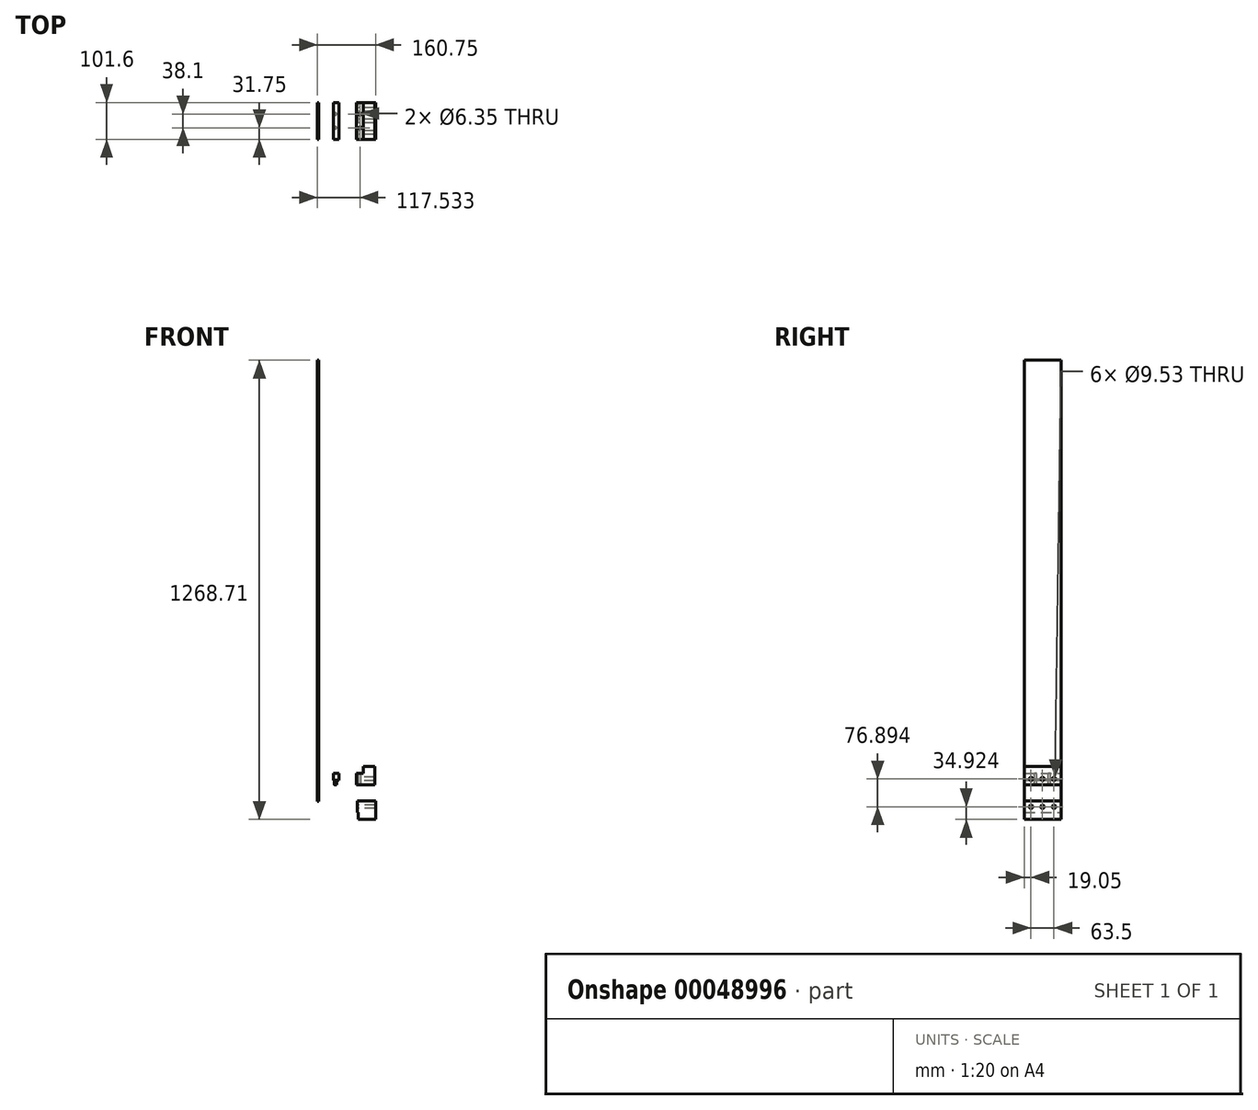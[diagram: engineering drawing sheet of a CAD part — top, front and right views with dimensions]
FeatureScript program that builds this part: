
annotation { "Feature Type Name" : "Feature", "Feature Type Description" : "" }
export const myFeature = defineFeature(function(context is Context, id is Id, definition is map)
    precondition{}
    {
        {
            var Q0;
            Q0=qCreatedBy(makeId("Front.planeOp"),FACE);
            var sketch = newSketch(context, id + "F0", { "sketchPlane" : qUnion([Q0])});
            skLineSegment(sketch, "E0", {"start": v(-61, 60.92) * mm, "end": v(-61, 29.17) * mm});
            skLineSegment(sketch, "E1", {"start": v(-61, 29.17) * mm, "end": v(-10.2, 29.17) * mm});
            skLineSegment(sketch, "E2", {"start": v(-10.2, 29.17) * mm, "end": v(-10.2, 79.97) * mm});
            skLineSegment(sketch, "E3", {"start": v(-10.2, 79.97) * mm, "end": v(-41.94, 79.97) * mm});
            skLineSegment(sketch, "E4", {"start": v(-41.94, 79.97) * mm, "end": v(-41.94, 60.92) * mm});
            skLineSegment(sketch, "E5", {"start": v(-41.94, 60.92) * mm, "end": v(-61, 60.92) * mm});
            skLineSegment(sketch, "E6", {"start": v(-59.05, -15.97) * mm, "end": v(-59.05, -47.72) * mm});
            skLineSegment(sketch, "E7", {"start": v(-59.05, -47.72) * mm, "end": v(-55.87, -47.72) * mm});
            skLineSegment(sketch, "E8", {"start": v(-55.87, -47.72) * mm, "end": v(-55.87, -66.77) * mm});
            skLineSegment(sketch, "E9", {"start": v(-55.87, -66.77) * mm, "end": v(-8.25, -66.77) * mm});
            skLineSegment(sketch, "E10", {"start": v(-8.25, -66.77) * mm, "end": v(-8.25, -15.97) * mm});
            skLineSegment(sketch, "E11", {"start": v(-8.25, -15.97) * mm, "end": v(-59.05, -15.97) * mm});
            skLineSegment(sketch, "E12.bottom", {"start": v(-125.4, 59.88) * mm, "end": v(-109.52, 59.88) * mm});
            skLineSegment(sketch, "E12.top", {"start": v(-125.4, 40.83) * mm, "end": v(-109.52, 40.83) * mm});
            skLineSegment(sketch, "E12.left", {"start": v(-125.4, 59.88) * mm, "end": v(-125.4, 40.83) * mm});
            skLineSegment(sketch, "E12.right", {"start": v(-109.52, 59.88) * mm, "end": v(-109.52, 40.83) * mm});
            skSolve(sketch);
        }
        {
            var Q0;
            Q0=makeQuery(id+"F0.imprint","IMPRINT",FACE,{"disambiguationData":[TD([[makeQuery(id+"F0.imprint","IMPRINT",EDGE,{"derivedFrom":sQuery(id+"F0.wireOp",EDGE,"E12.bottom")}),-1.0]])]});
            extrude(context, id + "F1", {"entities" : qUnion([Q0]), "depth" : 101.6 * mm});
        }
        {
            var Q0;
            Q0=makeQuery(id+"F0.imprint","IMPRINT",FACE,{"disambiguationData":[TD([[makeQuery(id+"F0.imprint","IMPRINT",EDGE,{"derivedFrom":sQuery(id+"F0.wireOp",EDGE,"E0")}),1.0]])]});
            extrude(context, id + "F2", {"entities" : qUnion([Q0]), "depth" : 101.6 * mm});
        }
        {
            var Q0;
            Q0=makeQuery(id+"F0.imprint","IMPRINT",FACE,{"disambiguationData":[TD([[makeQuery(id+"F0.imprint","IMPRINT",EDGE,{"derivedFrom":sQuery(id+"F0.wireOp",EDGE,"E6")}),1.0]])]});
            extrude(context, id + "F3", {"entities" : qUnion([Q0]), "depth" : 101.6 * mm});
        }
        {
            var Q0;
            Q0=makeQuery(id+"F2.opExtrude","SWEPT_FACE",FACE,{"disambiguationData":[OSD([sQuery(id+"F0.wireOp",EDGE,"E5")])]});
            var sketch = newSketch(context, id + "F4", { "sketchPlane" : qUnion([Q0])});
            skLineSegment(sketch, "E13.bottom", {"start": v(-61, -101.6) * mm, "end": v(-51.47, -101.6) * mm});
            skLineSegment(sketch, "E13.top", {"start": v(-61, -69.85) * mm, "end": v(-51.47, -69.85) * mm});
            skLineSegment(sketch, "E13.left", {"start": v(-61, -101.6) * mm, "end": v(-61, -69.85) * mm});
            skLineSegment(sketch, "E13.right", {"start": v(-51.47, -101.6) * mm, "end": v(-51.47, -69.85) * mm});
            skLineSegment(sketch, "E14.bottom", {"start": v(-61, 0) * mm, "end": v(-51.47, 0) * mm});
            skLineSegment(sketch, "E14.top", {"start": v(-61, -31.75) * mm, "end": v(-51.47, -31.75) * mm});
            skLineSegment(sketch, "E14.left", {"start": v(-61, 0) * mm, "end": v(-61, -31.75) * mm});
            skLineSegment(sketch, "E14.right", {"start": v(-51.47, 0) * mm, "end": v(-51.47, -31.75) * mm});
            skSolve(sketch);
        }
        {
            var Q0;
            Q0=sQuery(id+"F4.wireOp",VERTEX,"E14.top.end");
            var Q1;
            Q1=sQuery(id+"F4.wireOp",VERTEX,"E13.right.end");
            var Q2;
            Q2=makeQuery(id+"F2.opExtrude","SWEPT_BODY",BODY,{"disambiguationData":[OSD([sQuery(id+"F0.wireOp",EDGE,"E0"),sQuery(id+"F0.wireOp",EDGE,"E1"),sQuery(id+"F0.wireOp",EDGE,"E2"),sQuery(id+"F0.wireOp",EDGE,"E3"),sQuery(id+"F0.wireOp",EDGE,"E4"),sQuery(id+"F0.wireOp",EDGE,"E5")])]});
            hole(context, id + "F5", {"style" : HoleStyle.SIMPLE, "holeDiameter" : 6.35 * mm, "endStyle" : HoleEndStyle.THROUGH, "locations" : qUnion([Q0, Q1]), "scope" : qUnion([Q2])});
        }
        {
            var Q0;
            Q0=makeQuery(id+"F2.opExtrude","SWEPT_FACE",FACE,{"disambiguationData":[OSD([sQuery(id+"F0.wireOp",EDGE,"E0")])]});
            var sketch = newSketch(context, id + "F6", { "sketchPlane" : qUnion([Q0])});
            skLineSegment(sketch, "E15.bottom", {"start": v(101.6, 29.17) * mm, "end": v(50.8, 29.17) * mm});
            skLineSegment(sketch, "E15.top", {"start": v(101.6, 45.05) * mm, "end": v(50.8, 45.05) * mm});
            skLineSegment(sketch, "E15.left", {"start": v(101.6, 29.17) * mm, "end": v(101.6, 45.05) * mm});
            skLineSegment(sketch, "E15.right", {"start": v(50.8, 29.17) * mm, "end": v(50.8, 45.05) * mm});
            skLineSegment(sketch, "E16.bottom", {"start": v(101.6, 29.17) * mm, "end": v(82.55, 29.17) * mm});
            skLineSegment(sketch, "E16.top", {"start": v(101.6, 45.05) * mm, "end": v(82.55, 45.05) * mm});
            skLineSegment(sketch, "E16.right", {"start": v(82.55, 29.17) * mm, "end": v(82.55, 45.05) * mm});
            skLineSegment(sketch, "E17.bottom", {"start": v(0, 29.17) * mm, "end": v(19.05, 29.17) * mm});
            skLineSegment(sketch, "E17.top", {"start": v(0, 45.05) * mm, "end": v(19.05, 45.05) * mm});
            skLineSegment(sketch, "E17.left", {"start": v(0, 29.17) * mm, "end": v(0, 45.05) * mm});
            skLineSegment(sketch, "E17.right", {"start": v(19.05, 29.17) * mm, "end": v(19.05, 45.05) * mm});
            skSolve(sketch);
        }
        {
            var Q0;
            Q0=sQuery(id+"F6.wireOp",VERTEX,"E17.right.end");
            var Q1;
            Q1=sQuery(id+"F6.wireOp",VERTEX,"E15.right.end");
            var Q2;
            Q2=sQuery(id+"F6.wireOp",VERTEX,"E16.top.end");
            var Q3;
            Q3=makeQuery(id+"F2.opExtrude","SWEPT_BODY",BODY,{"disambiguationData":[OSD([sQuery(id+"F0.wireOp",EDGE,"E0"),sQuery(id+"F0.wireOp",EDGE,"E1"),sQuery(id+"F0.wireOp",EDGE,"E2"),sQuery(id+"F0.wireOp",EDGE,"E3"),sQuery(id+"F0.wireOp",EDGE,"E4"),sQuery(id+"F0.wireOp",EDGE,"E5")])]});
            hole(context, id + "F7", {"style" : HoleStyle.SIMPLE, "holeDiameter" : 9.52 * mm, "endStyle" : HoleEndStyle.THROUGH, "locations" : qUnion([Q0, Q1, Q2]), "scope" : qUnion([Q3])});
        }
        {
            var Q0;
            Q0=makeQuery(id+"F1.opExtrude","SWEPT_FACE",FACE,{"disambiguationData":[OSD([sQuery(id+"F0.wireOp",EDGE,"E12.top")])]});
            var sketch = newSketch(context, id + "F8", { "sketchPlane" : qUnion([Q0])});
            skLineSegment(sketch, "E18.bottom", {"start": v(-109.52, 101.6) * mm, "end": v(-119.04, 101.6) * mm});
            skLineSegment(sketch, "E18.left", {"start": v(-109.52, 101.6) * mm, "end": v(-109.52, 69.85) * mm});
            skLineSegment(sketch, "E19.bottom", {"start": v(-109.52, 0) * mm, "end": v(-119.04, 0) * mm});
            skLineSegment(sketch, "E19.left", {"start": v(-109.52, 0) * mm, "end": v(-109.52, 31.75) * mm});
            skCircle(sketch, "E20", {"center": v(-119.04, 69.85) * mm, "radius": 3.18 * mm});
            skCircle(sketch, "E21", {"center": v(-119.04, 31.75) * mm, "radius": 3.18 * mm});
            skSolve(sketch);
        }
        {
            var Q0;
            Q0=makeQuery(id+"F8.imprint","IMPRINT",FACE,{"disambiguationData":[TD([[makeQuery(id+"F8.imprint","IMPRINT",EDGE,{"derivedFrom":sQuery(id+"F8.wireOp",EDGE,"E20")}),1.0]])]});
            var Q1;
            Q1=makeQuery(id+"F8.imprint","IMPRINT",FACE,{"disambiguationData":[TD([[makeQuery(id+"F8.imprint","IMPRINT",EDGE,{"derivedFrom":sQuery(id+"F8.wireOp",EDGE,"E21")}),1.0]])]});
            extrude(context, id + "F9", {"entities" : qUnion([Q0, Q1]), "operationType" : NewBodyOperationType.ADD, "depth" : 12.7 * mm});
        }
        {
            var Q0;
            Q0=makeQuery(id+"F3.opExtrude","SWEPT_FACE",FACE,{"disambiguationData":[OSD([sQuery(id+"F0.wireOp",EDGE,"E6")])]});
            var sketch = newSketch(context, id + "F10", { "sketchPlane" : qUnion([Q0])});
            skLineSegment(sketch, "E22.bottom", {"start": v(101.6, -15.97) * mm, "end": v(50.8, -15.97) * mm});
            skLineSegment(sketch, "E22.top", {"start": v(101.6, -31.85) * mm, "end": v(50.8, -31.85) * mm});
            skLineSegment(sketch, "E22.left", {"start": v(101.6, -15.97) * mm, "end": v(101.6, -31.85) * mm});
            skLineSegment(sketch, "E22.right", {"start": v(50.8, -15.97) * mm, "end": v(50.8, -31.85) * mm});
            skLineSegment(sketch, "E23.bottom", {"start": v(101.6, -15.97) * mm, "end": v(82.55, -15.97) * mm});
            skLineSegment(sketch, "E23.top", {"start": v(101.6, -31.85) * mm, "end": v(82.55, -31.85) * mm});
            skLineSegment(sketch, "E23.right", {"start": v(82.55, -15.97) * mm, "end": v(82.55, -31.85) * mm});
            skLineSegment(sketch, "E24.bottom", {"start": v(0, -15.97) * mm, "end": v(19.05, -15.97) * mm});
            skLineSegment(sketch, "E24.top", {"start": v(0, -31.85) * mm, "end": v(19.05, -31.85) * mm});
            skLineSegment(sketch, "E24.left", {"start": v(0, -15.97) * mm, "end": v(0, -31.85) * mm});
            skLineSegment(sketch, "E24.right", {"start": v(19.05, -15.97) * mm, "end": v(19.05, -31.85) * mm});
            skSolve(sketch);
        }
        {
            var Q0;
            Q0=sQuery(id+"F10.wireOp",VERTEX,"E24.right.end");
            var Q1;
            Q1=sQuery(id+"F10.wireOp",VERTEX,"E22.top.end");
            var Q2;
            Q2=sQuery(id+"F10.wireOp",VERTEX,"E23.top.end");
            var Q3;
            Q3=makeQuery(id+"F3.opExtrude","SWEPT_BODY",BODY,{"disambiguationData":[OSD([sQuery(id+"F0.wireOp",EDGE,"E6"),sQuery(id+"F0.wireOp",EDGE,"E7"),sQuery(id+"F0.wireOp",EDGE,"E8"),sQuery(id+"F0.wireOp",EDGE,"E9"),sQuery(id+"F0.wireOp",EDGE,"E10"),sQuery(id+"F0.wireOp",EDGE,"E11")])]});
            hole(context, id + "F11", {"style" : HoleStyle.SIMPLE, "holeDiameter" : 9.52 * mm, "endStyle" : HoleEndStyle.THROUGH, "locations" : qUnion([Q0, Q1, Q2]), "scope" : qUnion([Q3])});
        }
        {
            var Q0;
            Q0=qCreatedBy(makeId("Front.planeOp"),FACE);
            var sketch = newSketch(context, id + "F12", { "sketchPlane" : qUnion([Q0])});
            skLineSegment(sketch, "E25.bottom", {"start": v(-169, 1201.94) * mm, "end": v(-165.83, 1201.94) * mm});
            skLineSegment(sketch, "E25.top", {"start": v(-169, -17.26) * mm, "end": v(-165.83, -17.26) * mm});
            skLineSegment(sketch, "E25.left", {"start": v(-169, 1201.94) * mm, "end": v(-169, -17.26) * mm});
            skLineSegment(sketch, "E25.right", {"start": v(-165.83, 1201.94) * mm, "end": v(-165.83, -17.26) * mm});
            skSolve(sketch);
        }
        {
            var Q0;
            Q0=makeQuery(id+"F12.imprint","IMPRINT",FACE,{"disambiguationData":[TD([[makeQuery(id+"F12.imprint","IMPRINT",EDGE,{"derivedFrom":sQuery(id+"F12.wireOp",EDGE,"E25.bottom")}),-1.0]])]});
            extrude(context, id + "F13", {"entities" : qUnion([Q0]), "depth" : 101.6 * mm});
        }
    });
